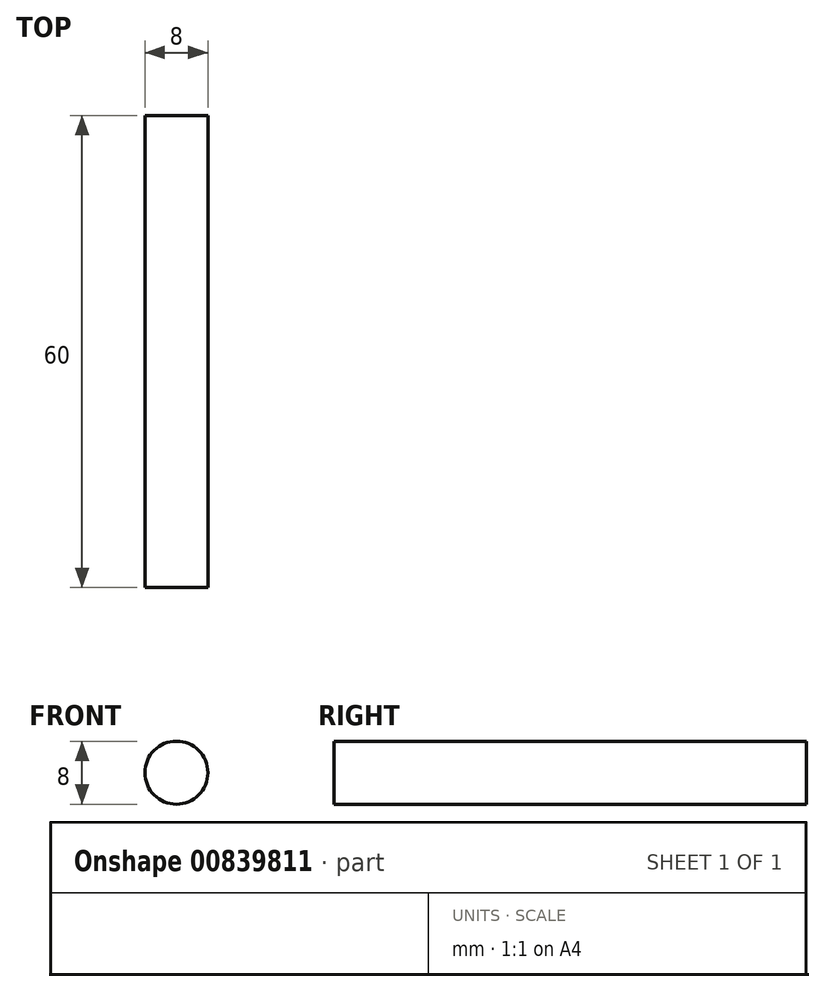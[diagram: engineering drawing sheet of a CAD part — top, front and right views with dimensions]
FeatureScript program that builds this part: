
annotation { "Feature Type Name" : "Feature", "Feature Type Description" : "" }
export const myFeature = defineFeature(function(context is Context, id is Id, definition is map)
    precondition{}
    {
        {
            var Q0;
            Q0=qCreatedBy(makeId("Front.planeOp"),FACE);
            var sketch = newSketch(context, id + "F0", { "sketchPlane" : qUnion([Q0])});
            skCircle(sketch, "E0", {"center": v(0, 0) * mm, "radius": 4 * mm});
            skSolve(sketch);
        }
        {
            var Q0;
            Q0=makeQuery(id+"F0.imprint","IMPRINT",FACE,{"disambiguationData":[TD([[makeQuery(id+"F0.imprint","IMPRINT",EDGE,{"derivedFrom":sQuery(id+"F0.wireOp",EDGE,"E0")}),1.0]])]});
            extrude(context, id + "F1", {"entities" : qUnion([Q0]), "depth" : 30 * mm, "offsetDistance" : 25 * mm, "hasSecondDirection" : true, "secondDirectionOppositeDirection" : true, "secondDirectionDepth" : 30 * mm});
        }
    });
